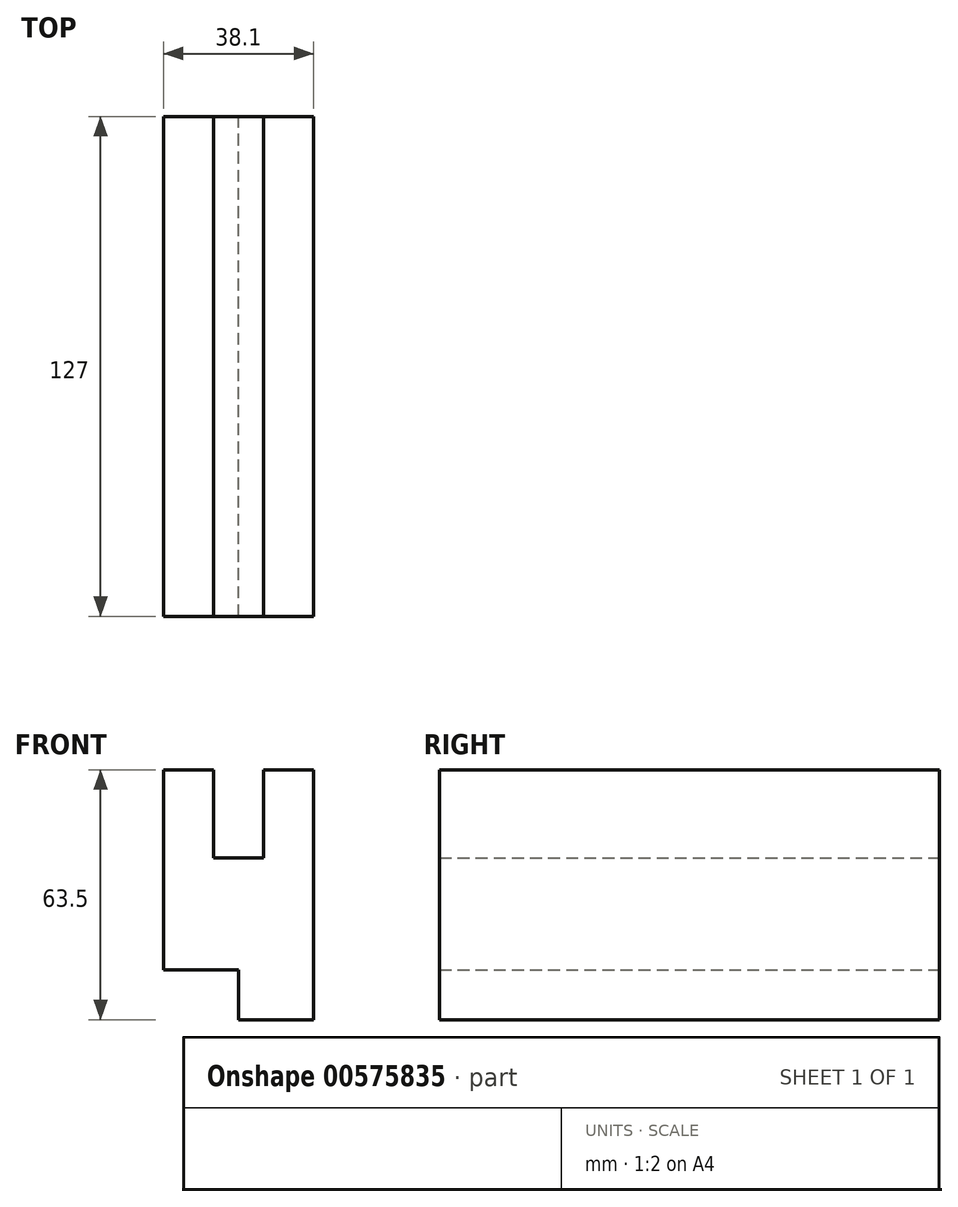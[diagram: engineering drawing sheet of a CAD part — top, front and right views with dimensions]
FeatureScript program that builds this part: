
annotation { "Feature Type Name" : "Feature", "Feature Type Description" : "" }
export const myFeature = defineFeature(function(context is Context, id is Id, definition is map)
    precondition{}
    {
        {
            var Q0;
            Q0=qCreatedBy(makeId("Front.planeOp"),FACE);
            var sketch = newSketch(context, id + "F0", { "sketchPlane" : qUnion([Q0])});
            skLineSegment(sketch, "E0", {"start": v(0, 0) * mm, "end": v(-19.05, 0) * mm});
            skLineSegment(sketch, "E1", {"start": v(-19.05, 0) * mm, "end": v(-19.05, 12.7) * mm});
            skLineSegment(sketch, "E2", {"start": v(-19.05, 12.7) * mm, "end": v(-38.1, 12.7) * mm});
            skLineSegment(sketch, "E3", {"start": v(-38.1, 12.7) * mm, "end": v(-38.1, 63.5) * mm});
            skLineSegment(sketch, "E4", {"start": v(-38.1, 63.5) * mm, "end": v(-25.4, 63.5) * mm});
            skLineSegment(sketch, "E5", {"start": v(-25.4, 63.5) * mm, "end": v(-25.4, 41.07) * mm});
            skLineSegment(sketch, "E6", {"start": v(-25.4, 41.07) * mm, "end": v(-12.7, 41.07) * mm});
            skLineSegment(sketch, "E7", {"start": v(-12.7, 41.07) * mm, "end": v(-12.7, 63.5) * mm});
            skLineSegment(sketch, "E8", {"start": v(-12.7, 63.5) * mm, "end": v(0, 63.5) * mm});
            skLineSegment(sketch, "E9", {"start": v(0, 63.5) * mm, "end": v(0, 0) * mm});
            skSolve(sketch);
        }
        {
            var Q0;
            Q0 = qSketchRegion(id + "F0", true);
            extrude(context, id + "F1", {"entities" : qUnion([Q0]), "depth" : 127 * mm, "offsetDistance" : 25.4 * mm});
        }
    });
